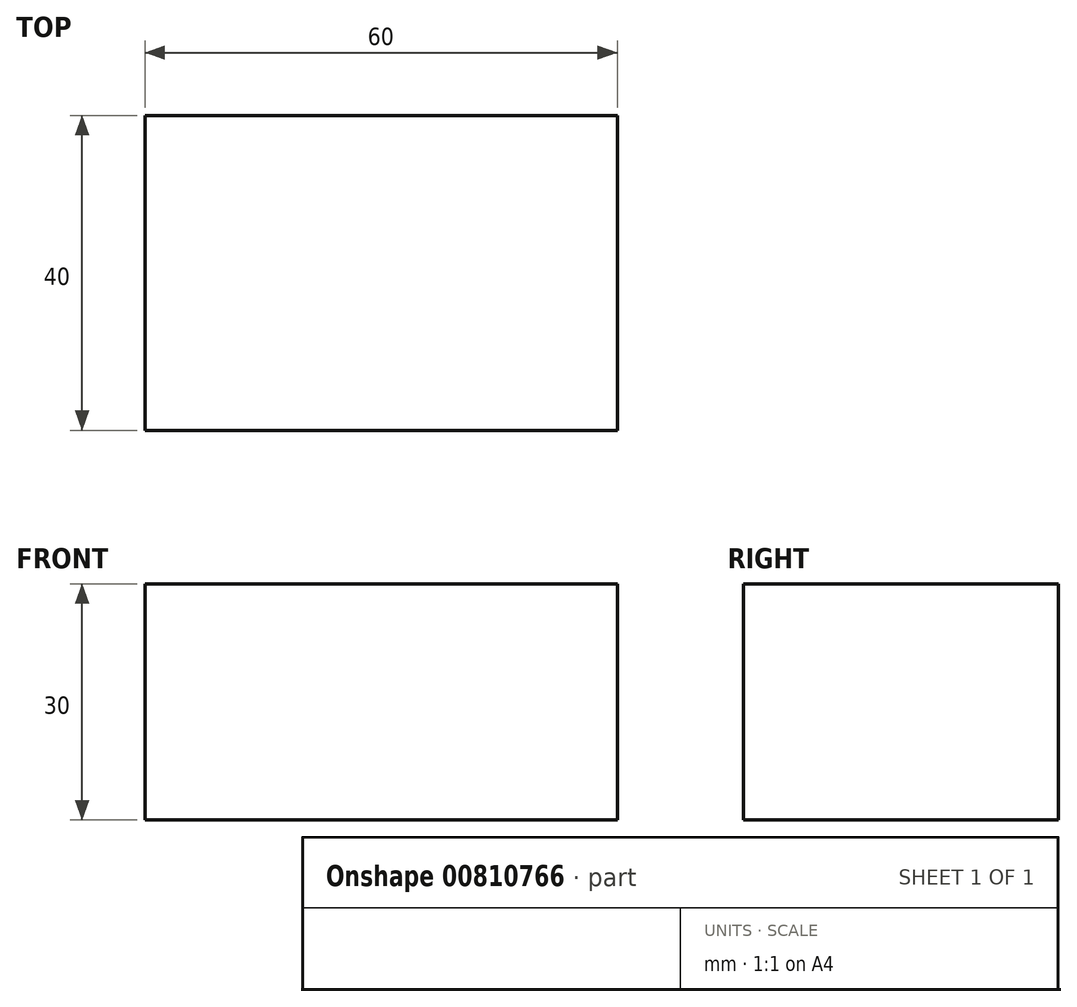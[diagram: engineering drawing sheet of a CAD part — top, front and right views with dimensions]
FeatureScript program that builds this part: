
annotation { "Feature Type Name" : "Feature", "Feature Type Description" : "" }
export const myFeature = defineFeature(function(context is Context, id is Id, definition is map)
    precondition{}
    {
        {
            var Q0;
            Q0=qCreatedBy(makeId("Right.planeOp"),FACE);
            var sketch = newSketch(context, id + "F0", { "sketchPlane" : qUnion([Q0])});
            skLineSegment(sketch, "E0.bottom", {"start": v(0, 0) * mm, "end": v(40, 0) * mm});
            skLineSegment(sketch, "E0.top", {"start": v(0, 30) * mm, "end": v(40, 30) * mm});
            skLineSegment(sketch, "E0.left", {"start": v(0, 0) * mm, "end": v(0, 30) * mm});
            skLineSegment(sketch, "E0.right", {"start": v(40, 0) * mm, "end": v(40, 30) * mm});
            skSolve(sketch);
        }
        {
            var Q0;
            Q0=qSketchRegion(id+"F0",true);
            extrude(context, id + "F1", {"entities" : qUnion([Q0]), "depth" : 60 * mm});
        }
    });
